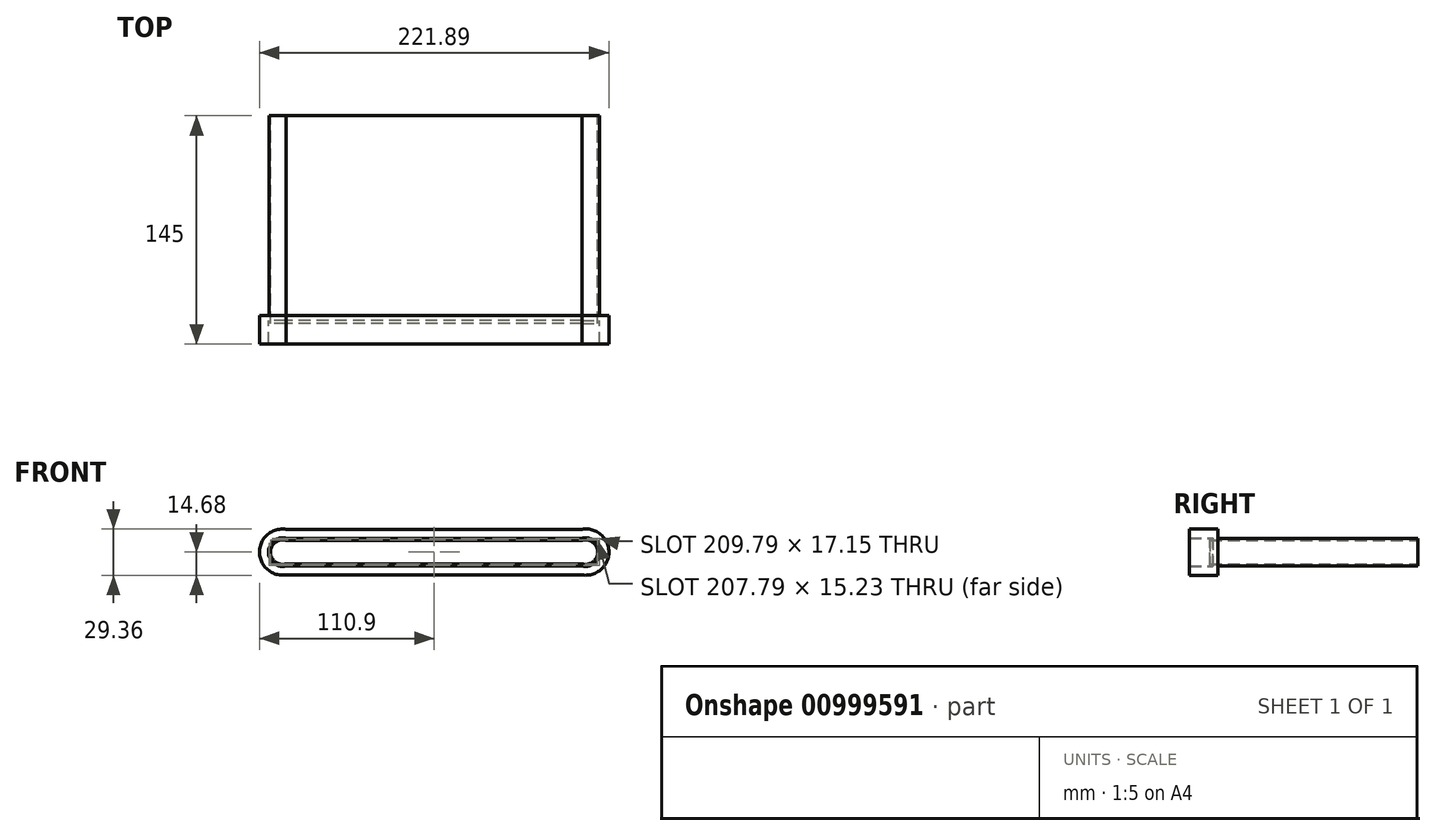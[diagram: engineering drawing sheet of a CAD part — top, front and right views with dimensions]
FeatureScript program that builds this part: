
annotation { "Feature Type Name" : "Feature", "Feature Type Description" : "" }
export const myFeature = defineFeature(function(context is Context, id is Id, definition is map)
    precondition{}
    {
        {
            var Q0;
            Q0=qCreatedBy(makeId("Front.planeOp"),FACE);
            var sketch = newSketch(context, id + "F0", { "sketchPlane" : qUnion([Q0])});
            skLineSegment(sketch, "E0.bottom", {"start": v(105, 8.5) * mm, "end": v(-105, 8.5) * mm});
            skLineSegment(sketch, "E0.top", {"start": v(105, -8.5) * mm, "end": v(-105, -8.5) * mm});
            skLineSegment(sketch, "E0.left", {"start": v(105, 8.5) * mm, "end": v(105, -8.5) * mm});
            skLineSegment(sketch, "E0.right", {"start": v(-105, 8.5) * mm, "end": v(-105, -8.5) * mm});
            skPoint(sketch, "E0.middle", {"position": v(0, 0) * mm});
            skLineSegment(sketch, "E1", {"start": v(0, -8.5) * mm, "end": v(94, -8.5) * mm});
            skLineSegment(sketch, "E2", {"start": v(94, -8.5) * mm, "end": v(-94, -8.5) * mm});
            skLineSegment(sketch, "E3", {"start": v(0, 8.5) * mm, "end": v(94, 8.5) * mm});
            skLineSegment(sketch, "E4", {"start": v(94, 8.5) * mm, "end": v(-94, 8.5) * mm});
            skArc(sketch, "E5", {"start": v(-94, 8.5) * mm, "mid": v(-104.89, 0) * mm, "end": v(-94, -8.5) * mm});
            skArc(sketch, "E6", {"start": v(94, -8.5) * mm, "mid": v(104.9, 0) * mm, "end": v(94, 8.5) * mm});
            skLineSegment(sketch, "E7", {"start": v(94, 8.5) * mm, "end": v(94, 14.5) * mm});
            skLineSegment(sketch, "E8", {"start": v(94, -8.5) * mm, "end": v(94, -14.5) * mm});
            skLineSegment(sketch, "E9", {"start": v(-94, 8.5) * mm, "end": v(-94, 14.5) * mm});
            skLineSegment(sketch, "E10", {"start": v(-94, -8.5) * mm, "end": v(-94, -14.5) * mm});
            skLineSegment(sketch, "E11", {"start": v(-94, -14.5) * mm, "end": v(94, -14.5) * mm});
            skLineSegment(sketch, "E12", {"start": v(94, 14.5) * mm, "end": v(-94, 14.5) * mm});
            skLineSegment(sketch, "E13", {"start": v(-104.89, 0) * mm, "end": v(-110.89, 0) * mm});
            skLineSegment(sketch, "E14", {"start": v(105, 0) * mm, "end": v(111, 0) * mm});
            skArc(sketch, "E15", {"start": v(-94, 14.5) * mm, "mid": v(-110.89, 0) * mm, "end": v(-94, -14.5) * mm});
            skArc(sketch, "E16", {"start": v(94, -14.5) * mm, "mid": v(111, 0) * mm, "end": v(94, 14.5) * mm});
            skSolve(sketch);
        }
        {
            var Q0;
            {var subQ0=sQuery(id+"F0.wireOp",EDGE,"E6");var subQ1=sQuery(id+"F0.wireOp",EDGE,"E0.bottom");var subQ3=makeQuery(id+"F0.imprint","INTERSECT",VERTEX,{"derivedFrom":[subQ1,subQ0]});Q0=makeQuery(id+"F0.imprint","IMPRINT",FACE,{"disambiguationData":[TD([[makeQuery(id+"F0.imprint","IMPRINT",EDGE,{"disambiguationData":[TD([[subQ3,-1.0]])],"derivedFrom":subQ1}),-1.0]])]});}
            var Q1;
            {var subQ0=sQuery(id+"F0.wireOp",EDGE,"E5");var subQ1=sQuery(id+"F0.wireOp",EDGE,"E0.bottom");var subQ2=makeQuery(id+"F0.imprint","INTERSECT",VERTEX,{"derivedFrom":[subQ1,subQ0]});Q1=makeQuery(id+"F0.imprint","IMPRINT",FACE,{"disambiguationData":[TD([[makeQuery(id+"F0.imprint","IMPRINT",EDGE,{"disambiguationData":[TD([[subQ2,1.0]])],"derivedFrom":subQ1}),-1.0]])]});}
            var Q2;
            {var subQ0=sQuery(id+"F0.wireOp",EDGE,"E6");var subQ1=sQuery(id+"F0.wireOp",EDGE,"E0.top");var subQ3=makeQuery(id+"F0.imprint","INTERSECT",VERTEX,{"derivedFrom":[subQ1,subQ0]});Q2=makeQuery(id+"F0.imprint","IMPRINT",FACE,{"disambiguationData":[TD([[makeQuery(id+"F0.imprint","IMPRINT",EDGE,{"disambiguationData":[TD([[subQ3,-1.0]])],"derivedFrom":subQ1}),1.0]])]});}
            var Q3;
            {var subQ0=sQuery(id+"F0.wireOp",EDGE,"E5");var subQ1=sQuery(id+"F0.wireOp",EDGE,"E0.top");var subQ2=makeQuery(id+"F0.imprint","INTERSECT",VERTEX,{"derivedFrom":[subQ1,subQ0]});Q3=makeQuery(id+"F0.imprint","IMPRINT",FACE,{"disambiguationData":[TD([[makeQuery(id+"F0.imprint","IMPRINT",EDGE,{"disambiguationData":[TD([[subQ2,1.0]])],"derivedFrom":subQ1}),1.0]])]});}
            var Q4;
            {var subQ9=sQuery(id+"F0.wireOp",EDGE,"E0.bottom");var subQ12=makeQuery(id+"F0.imprint","IMPRINT",VERTEX,{"derivedFrom":subQ9});Q4=makeQuery(id+"F0.imprint","IMPRINT",FACE,{"disambiguationData":[TD([[makeQuery(id+"F0.imprint","IMPRINT",EDGE,{"disambiguationData":[TD([[subQ12,1.0]])],"derivedFrom":subQ9}),1.0]])]});}
            extrude(context, id + "F1", {"entities" : qUnion([Q0, Q1, Q2, Q3, Q4]), "depth" : 2 * mm, "offsetDistance" : 25 * mm, "hasSecondDirection" : true, "secondDirectionOppositeDirection" : true, "secondDirectionDepth" : 130 * mm});
        }
        {
            var Q0;
            Q0=makeQuery(id+"F1.opExtrude","CAP_FACE",FACE,{"disambiguationData":[OSD([sQuery(id+"F0.wireOp",EDGE,"E0.bottom"),sQuery(id+"F0.wireOp",EDGE,"E0.top"),sQuery(id+"F0.wireOp",EDGE,"E5"),sQuery(id+"F0.wireOp",EDGE,"E6")])],"isStart":false});
            var Q1;
            Q1=makeQuery(id+"F1.opExtrude","CAP_FACE",FACE,{"disambiguationData":[OSD([sQuery(id+"F0.wireOp",EDGE,"E0.bottom"),sQuery(id+"F0.wireOp",EDGE,"E0.top"),sQuery(id+"F0.wireOp",EDGE,"E5"),sQuery(id+"F0.wireOp",EDGE,"E6")])],"isStart":true});
            shell(context, id + "F2", {"entities" : qUnion([Q0, Q1]), "thickness" : 1 * mm});
        }
        {
            var Q0;
            {var subQ0=sQuery(id+"F0.wireOp",EDGE,"E7");Q0=makeQuery(id+"F0.imprint","IMPRINT",FACE,{"disambiguationData":[TD([[makeQuery(id+"F0.imprint","IMPRINT",EDGE,{"derivedFrom":subQ0}),1.0]])]});}
            var Q1;
            {var subQ0=sQuery(id+"F0.wireOp",EDGE,"E7");Q1=makeQuery(id+"F0.imprint","IMPRINT",FACE,{"disambiguationData":[TD([[makeQuery(id+"F0.imprint","IMPRINT",EDGE,{"derivedFrom":subQ0}),-1.0]])]});}
            var Q2;
            {var subQ0=sQuery(id+"F0.wireOp",EDGE,"E8");Q2=makeQuery(id+"F0.imprint","IMPRINT",FACE,{"disambiguationData":[TD([[makeQuery(id+"F0.imprint","IMPRINT",EDGE,{"derivedFrom":subQ0}),-1.0]])]});}
            var Q3;
            {var subQ0=sQuery(id+"F0.wireOp",EDGE,"E8");Q3=makeQuery(id+"F0.imprint","IMPRINT",FACE,{"disambiguationData":[TD([[makeQuery(id+"F0.imprint","IMPRINT",EDGE,{"derivedFrom":subQ0}),1.0]])]});}
            var Q4;
            {var subQ0=sQuery(id+"F0.wireOp",EDGE,"E0.left");var subQ1=sQuery(id+"F0.wireOp",EDGE,"E0.bottom");var subQ2=makeQuery(id+"F0.imprint","INTERSECT",VERTEX,{"derivedFrom":[subQ1,subQ0]});Q4=makeQuery(id+"F0.imprint","IMPRINT",FACE,{"disambiguationData":[TD([[makeQuery(id+"F0.imprint","IMPRINT",EDGE,{"disambiguationData":[TD([[subQ2,-1.0]])],"derivedFrom":subQ1}),1.0]])]});}
            var Q5;
            {var subQ0=sQuery(id+"F0.wireOp",EDGE,"E9");Q5=makeQuery(id+"F0.imprint","IMPRINT",FACE,{"disambiguationData":[TD([[makeQuery(id+"F0.imprint","IMPRINT",EDGE,{"derivedFrom":subQ0}),1.0]])]});}
            var Q6;
            {var subQ0=sQuery(id+"F0.wireOp",EDGE,"E5");var subQ1=sQuery(id+"F0.wireOp",EDGE,"E0.bottom");var subQ2=makeQuery(id+"F0.imprint","INTERSECT",VERTEX,{"derivedFrom":[subQ1,subQ0]});Q6=makeQuery(id+"F0.imprint","IMPRINT",FACE,{"disambiguationData":[TD([[makeQuery(id+"F0.imprint","IMPRINT",EDGE,{"disambiguationData":[TD([[subQ2,-1.0]])],"derivedFrom":subQ1}),1.0]])]});}
            var Q7;
            {var subQ0=sQuery(id+"F0.wireOp",EDGE,"E10");Q7=makeQuery(id+"F0.imprint","IMPRINT",FACE,{"disambiguationData":[TD([[makeQuery(id+"F0.imprint","IMPRINT",EDGE,{"derivedFrom":subQ0}),-1.0]])]});}
            var Q8;
            {var subQ0=sQuery(id+"F0.wireOp",EDGE,"E5");var subQ1=sQuery(id+"F0.wireOp",EDGE,"E0.top");var subQ2=makeQuery(id+"F0.imprint","INTERSECT",VERTEX,{"derivedFrom":[subQ1,subQ0]});Q8=makeQuery(id+"F0.imprint","IMPRINT",FACE,{"disambiguationData":[TD([[makeQuery(id+"F0.imprint","IMPRINT",EDGE,{"disambiguationData":[TD([[subQ2,-1.0]])],"derivedFrom":subQ1}),-1.0]])]});}
            extrude(context, id + "F3", {"entities" : qUnion([Q0, Q1, Q2, Q3, Q4, Q5, Q6, Q7, Q8]), "operationType" : NewBodyOperationType.ADD, "oppositeDirection" : true, "depth" : 3 * mm, "offsetDistance" : 25 * mm});
        }
        {
            var Q0;
            Q0=makeQuery(id+"F3.opExtrude","CAP_FACE",FACE,{"disambiguationData":[OSD([sQuery(id+"F0.wireOp",EDGE,"E0.bottom"),sQuery(id+"F0.wireOp",EDGE,"E0.top"),sQuery(id+"F0.wireOp",EDGE,"E5"),sQuery(id+"F0.wireOp",EDGE,"E6"),sQuery(id+"F0.wireOp",EDGE,"E11"),sQuery(id+"F0.wireOp",EDGE,"E12"),sQuery(id+"F0.wireOp",EDGE,"E15"),sQuery(id+"F0.wireOp",EDGE,"E16")])],"isStart":true});
            var sketch = newSketch(context, id + "F4", { "sketchPlane" : qUnion([Q0])});
            skLineSegment(sketch, "E17", {"start": v(-94, 8.5) * mm, "end": v(-94, 8.8) * mm});
            skLineSegment(sketch, "E18", {"start": v(-94, -8.5) * mm, "end": v(-94, -8.8) * mm});
            skLineSegment(sketch, "E19", {"start": v(-104.89, 0) * mm, "end": v(-105.19, 0) * mm});
            skArc(sketch, "E20", {"start": v(-94, 8.8) * mm, "mid": v(-105.19, 0) * mm, "end": v(-94, -8.8) * mm});
            skLineSegment(sketch, "E21", {"start": v(94, -8.5) * mm, "end": v(94, -8.8) * mm});
            skLineSegment(sketch, "E22", {"start": v(104.9, 0) * mm, "end": v(105.2, 0) * mm});
            skLineSegment(sketch, "E23", {"start": v(94, 8.5) * mm, "end": v(94, 8.8) * mm});
            skArc(sketch, "E24", {"start": v(94, -8.8) * mm, "mid": v(105.2, 0) * mm, "end": v(94, 8.8) * mm});
            skLineSegment(sketch, "E25", {"start": v(94, -8.8) * mm, "end": v(-94, -8.8) * mm});
            skLineSegment(sketch, "E26", {"start": v(-94, 8.8) * mm, "end": v(94, 8.8) * mm});
            skSolve(sketch);
        }
        {
            var Q0;
            {var subQ3=sQuery(id+"F4.wireOp",EDGE,"E25");Q0=makeQuery(id+"F4.imprint","IMPRINT",FACE,{"disambiguationData":[TD([[makeQuery(id+"F4.imprint","IMPRINT",EDGE,{"derivedFrom":subQ3}),1.0]])]});}
            extrude(context, id + "F5", {"entities" : qUnion([Q0]), "operationType" : NewBodyOperationType.ADD, "depth" : 15 * mm, "offsetDistance" : 25 * mm});
        }
    });
